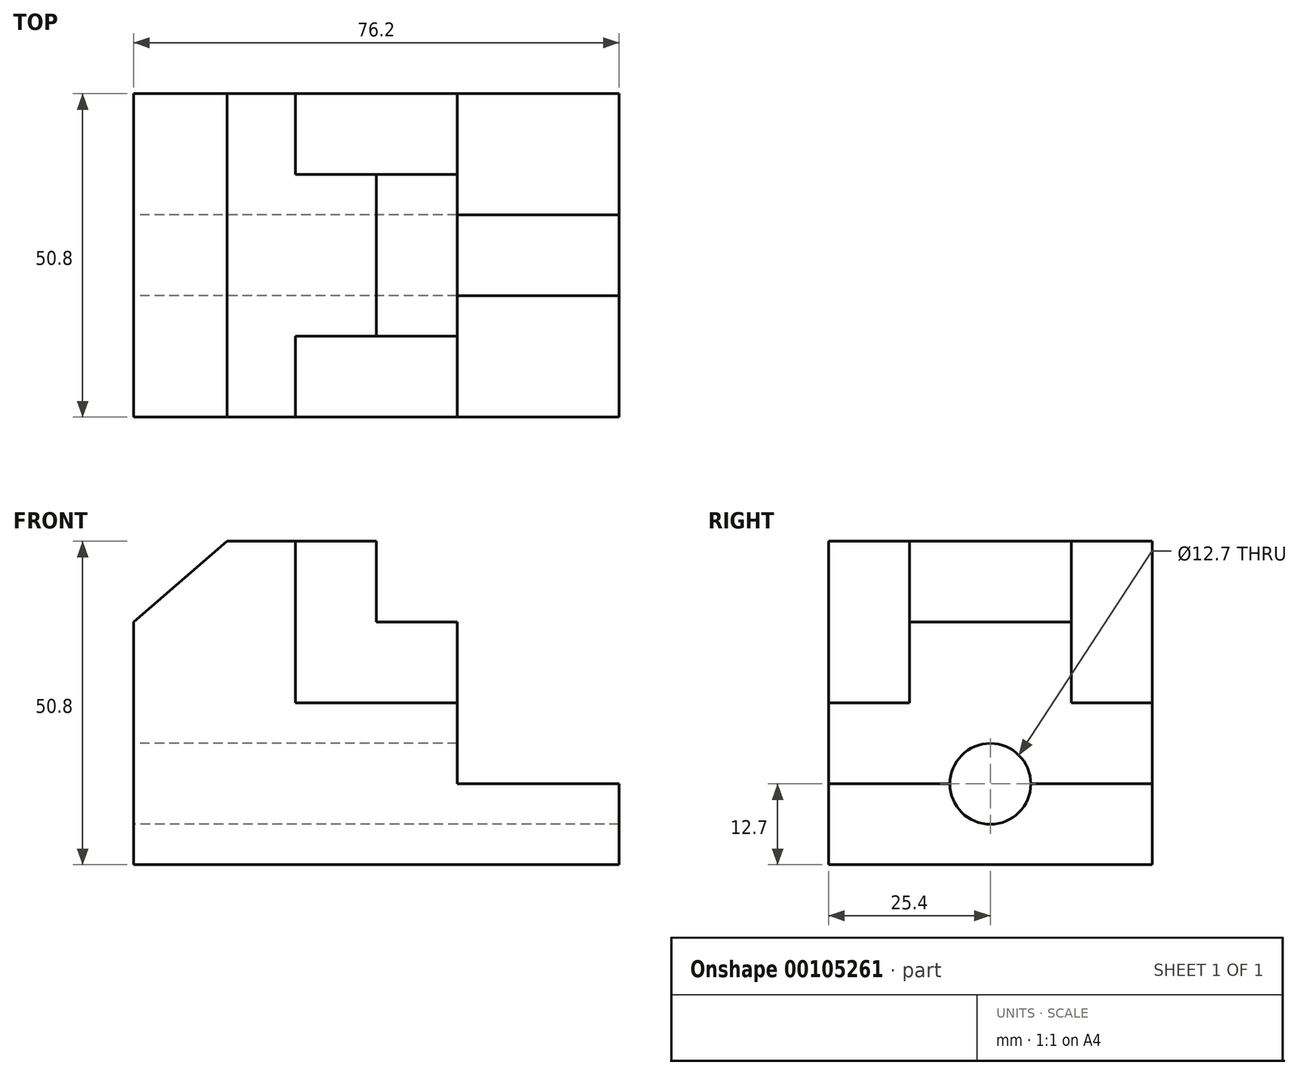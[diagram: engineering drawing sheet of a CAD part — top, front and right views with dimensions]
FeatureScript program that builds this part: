
annotation { "Feature Type Name" : "Feature", "Feature Type Description" : "" }
export const myFeature = defineFeature(function(context is Context, id is Id, definition is map)
    precondition{}
    {
        {
            var Q0;
            Q0=qCreatedBy(makeId("Front.planeOp"),FACE);
            var sketch = newSketch(context, id + "F0", { "sketchPlane" : qUnion([Q0])});
            skLineSegment(sketch, "E0", {"start": v(0, 0) * mm, "end": v(0, 38.1) * mm});
            skLineSegment(sketch, "E1", {"start": v(0, 38.1) * mm, "end": v(14.67, 50.8) * mm});
            skLineSegment(sketch, "E2", {"start": v(14.67, 50.8) * mm, "end": v(38.1, 50.8) * mm});
            skLineSegment(sketch, "E3", {"start": v(38.1, 50.8) * mm, "end": v(38.1, 38.1) * mm});
            skLineSegment(sketch, "E4", {"start": v(38.1, 38.1) * mm, "end": v(50.8, 38.1) * mm});
            skLineSegment(sketch, "E5", {"start": v(50.8, 38.1) * mm, "end": v(50.8, 12.7) * mm});
            skLineSegment(sketch, "E6", {"start": v(50.8, 12.7) * mm, "end": v(76.2, 12.7) * mm});
            skLineSegment(sketch, "E7", {"start": v(76.2, 12.7) * mm, "end": v(76.2, 0) * mm});
            skLineSegment(sketch, "E8", {"start": v(76.2, 0) * mm, "end": v(0, 0) * mm});
            skSolve(sketch);
        }
        {
            var Q0;
            Q0 = qSketchRegion(id + "F0", true);
            extrude(context, id + "F1", {"entities" : qUnion([Q0]), "depth" : 50.8 * mm});
        }
        {
            var Q0;
            Q0=qCreatedBy(makeId("Front.planeOp"),FACE);
            var sketch = newSketch(context, id + "F2", { "sketchPlane" : qUnion([Q0])});
            skLineSegment(sketch, "E9", {"start": v(25.4, 50.8) * mm, "end": v(25.4, 25.4) * mm});
            skLineSegment(sketch, "E10", {"start": v(25.4, 25.4) * mm, "end": v(50.8, 25.4) * mm});
            skLineSegment(sketch, "E11", {"start": v(25.4, 50.8) * mm, "end": v(38.1, 50.8) * mm});
            skLineSegment(sketch, "E12", {"start": v(38.1, 50.8) * mm, "end": v(38.1, 38.1) * mm});
            skLineSegment(sketch, "E13", {"start": v(38.1, 38.1) * mm, "end": v(50.8, 38.1) * mm});
            skLineSegment(sketch, "E14", {"start": v(50.8, 38.1) * mm, "end": v(50.8, 25.4) * mm});
            skSolve(sketch);
        }
        {
            var Q0;
            Q0 = qSketchRegion(id + "F2", true);
            extrude(context, id + "F3", {"entities" : qUnion([Q0]), "operationType" : NewBodyOperationType.REMOVE, "depth" : 12.7 * mm});
        }
        {
            var Q0;
            Q0=qCreatedBy(makeId("Front.planeOp"),FACE);
            var sketch = newSketch(context, id + "F4", { "sketchPlane" : qUnion([Q0])});
            skLineSegment(sketch, "E15", {"start": v(25.4, 50.8) * mm, "end": v(38.1, 50.8) * mm});
            skLineSegment(sketch, "E16", {"start": v(38.1, 50.8) * mm, "end": v(38.1, 38.1) * mm});
            skLineSegment(sketch, "E17", {"start": v(38.1, 38.1) * mm, "end": v(50.8, 38.1) * mm});
            skLineSegment(sketch, "E18", {"start": v(50.8, 38.1) * mm, "end": v(50.8, 25.4) * mm});
            skLineSegment(sketch, "E19", {"start": v(50.8, 25.4) * mm, "end": v(25.4, 25.4) * mm});
            skLineSegment(sketch, "E20", {"start": v(25.4, 25.4) * mm, "end": v(25.4, 50.8) * mm});
            skSolve(sketch);
        }
        {
            var Q0;
            Q0=makeQuery(id+"F4.imprint","IMPRINT",FACE,{"disambiguationData":[TD([[makeQuery(id+"F4.imprint","IMPRINT",EDGE,{"derivedFrom":sQuery(id+"F4.wireOp",EDGE,"E15")}),-1.0]])]});
            extrude(context, id + "F5", {"entities" : qUnion([Q0]), "operationType" : NewBodyOperationType.REMOVE, "endBound" : BoundingType.THROUGH_ALL, "depth" : 25.4 * mm, "hasSecondDirection" : true, "secondDirectionOppositeDirection" : false, "secondDirectionDepth" : 38.1 * mm});
        }
        {
            var Q0;
            Q0=qCreatedBy(makeId("Right.planeOp"),FACE);
            var sketch = newSketch(context, id + "F6", { "sketchPlane" : qUnion([Q0])});
            skCircle(sketch, "E21", {"center": v(-25.4, 12.7) * mm, "radius": 6.35 * mm});
            skSolve(sketch);
        }
        {
            var Q0;
            Q0 = qSketchRegion(id + "F6", true);
            extrude(context, id + "F7", {"entities" : qUnion([Q0]), "operationType" : NewBodyOperationType.REMOVE, "endBound" : BoundingType.THROUGH_ALL, "depth" : 25.4 * mm});
        }
    });
